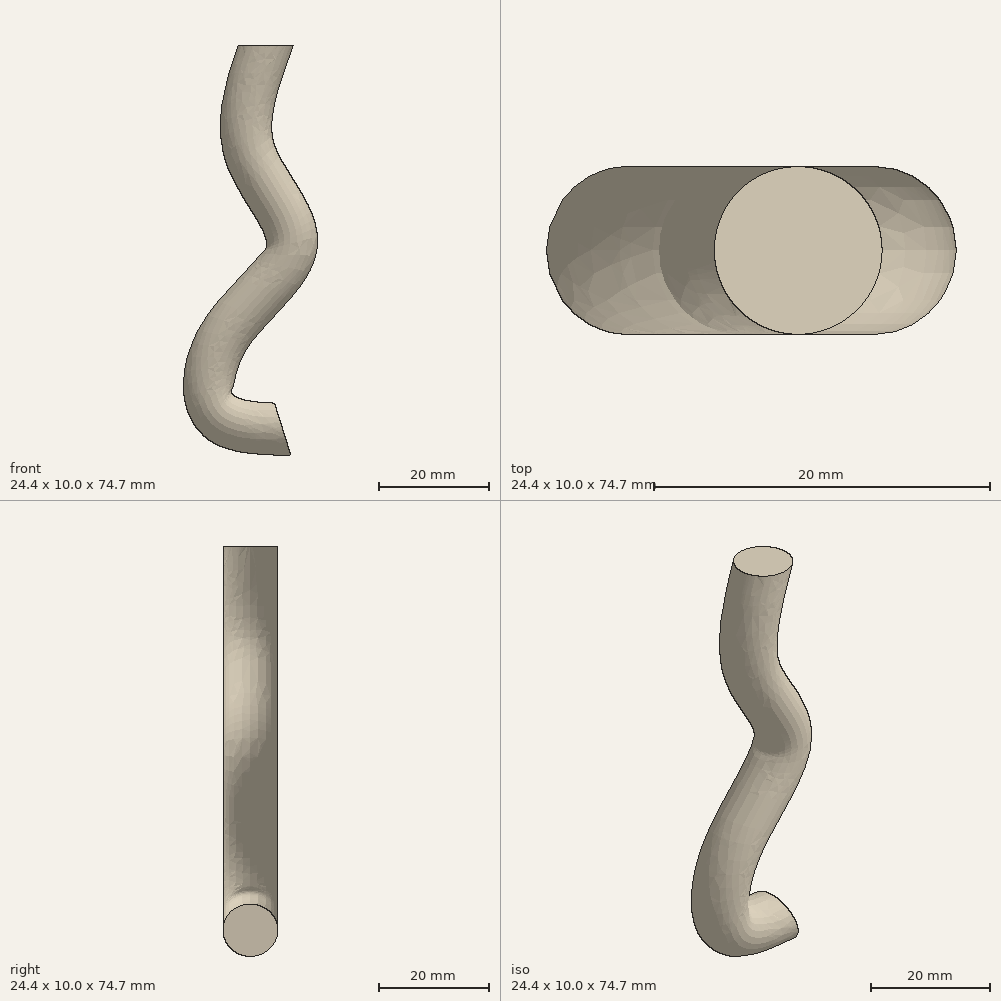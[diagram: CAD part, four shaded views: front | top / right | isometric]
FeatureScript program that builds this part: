
annotation { "Feature Type Name" : "Feature", "Feature Type Description" : "" }
export const myFeature = defineFeature(function(context is Context, id is Id, definition is map)
    precondition{}
    {
        {
            var Q0;
            Q0=qCreatedBy(makeId("Top.planeOp"),FACE);
            var sketch = newSketch(context, id + "F0", { "sketchPlane" : qUnion([Q0])});
            skCircle(sketch, "E0", {"center": v(0, 0) * mm, "radius": 5 * mm});
            skSolve(sketch);
        }
        {
            var Q0;
            Q0=qCreatedBy(makeId("Front.planeOp"),FACE);
            var sketch = newSketch(context, id + "F1", { "sketchPlane" : qUnion([Q0])});
            skFitSpline(sketch, "E1", {"points": [v(0, 0) * mm, v(-2.77, -19.68) * mm, v(4.57, -36.16) * mm, v(-7.45, -52.97) * mm, v(-8.72, -66.8) * mm, v(3.08, -69.88) * mm], "startDerivative": vector(-32.82, -92.76) * mm, "endDerivative": vector(84.14, -3.1) * mm});
            skSolve(sketch);
        }
        {
            var Q0;
            Q0=makeQuery(id+"F0.imprint","IMPRINT",FACE,{"disambiguationData":[TD([[makeQuery(id+"F0.imprint","IMPRINT",EDGE,{"derivedFrom":sQuery(id+"F0.wireOp",EDGE,"E0")}),1.0]])]});
            var Q1;
            Q1=sQuery(id+"F1.wireOp",EDGE,"E1");
            sweep(context, id + "F2", {"profiles" : qUnion([Q0]), "path" : qUnion([Q1])});
        }
    });
